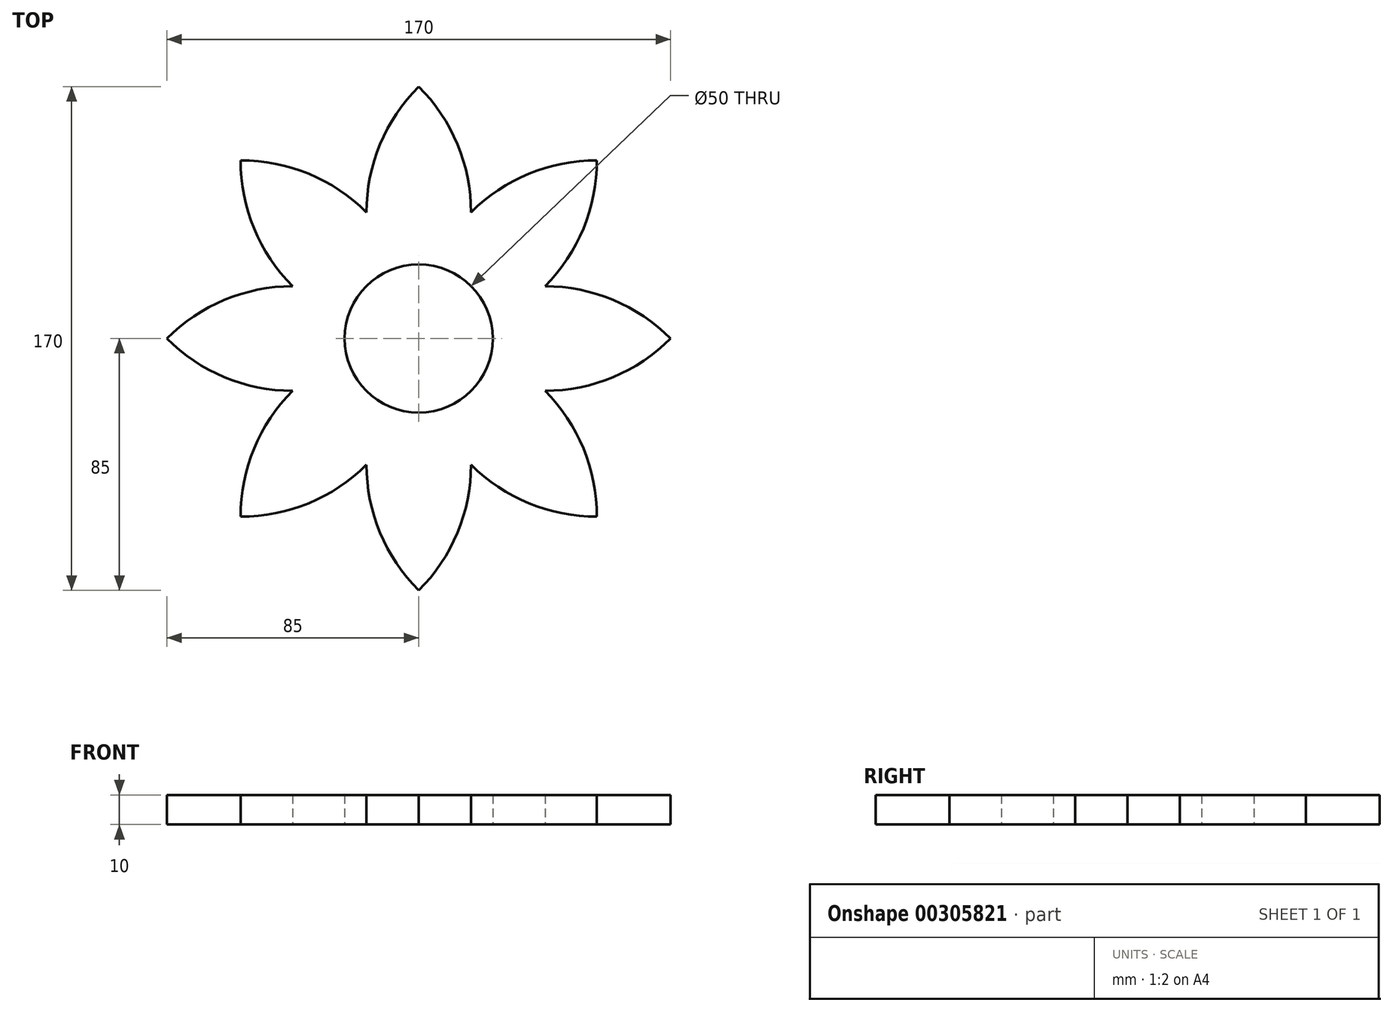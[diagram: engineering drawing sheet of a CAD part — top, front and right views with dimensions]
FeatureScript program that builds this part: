
annotation { "Feature Type Name" : "Feature", "Feature Type Description" : "" }
export const myFeature = defineFeature(function(context is Context, id is Id, definition is map)
    precondition{}
    {
        {
            var Q0;
            Q0=qCreatedBy(makeId("Top.planeOp"),FACE);
            var sketch = newSketch(context, id + "F0", { "sketchPlane" : qUnion([Q0])});
            skCircle(sketch, "E0", {"center": v(0, 0) * mm, "radius": 25 * mm});
            skLineSegment(sketch, "E1", {"start": v(0, 25) * mm, "end": v(0, 85) * mm});
            skArc(sketch, "E2", {"start": v(0, 85) * mm, "mid": v(-17.65, 42.5) * mm, "end": v(0, 0) * mm});
            skArc(sketch, "E3.MirrorCS", {"start": v(0, 85) * mm, "mid": v(17.65, 42.5) * mm, "end": v(0, 0) * mm});
            skArc(sketch, "E4.1.0", {"start": v(-60.1, 60.1) * mm, "mid": v(-17.57, 42.53) * mm, "end": v(0, 0) * mm});
            skLineSegment(sketch, "E4.1.1", {"start": v(-17.68, 17.68) * mm, "end": v(-60.1, 60.1) * mm});
            skArc(sketch, "E4.1.2", {"start": v(-60.1, 60.1) * mm, "mid": v(-42.53, 17.57) * mm, "end": v(0, 0) * mm});
            skArc(sketch, "E4.1.3", {"start": v(-60.1, 60.1) * mm, "mid": v(-17.57, 42.53) * mm, "end": v(0, 0) * mm});
            skArc(sketch, "E4.2.0", {"start": v(-85, 0) * mm, "mid": v(-42.5, 17.65) * mm, "end": v(0, 0) * mm});
            skLineSegment(sketch, "E4.2.1", {"start": v(-25, 0) * mm, "end": v(-85, 0) * mm});
            skArc(sketch, "E4.2.2", {"start": v(-85, 0) * mm, "mid": v(-42.5, -17.65) * mm, "end": v(0, 0) * mm});
            skArc(sketch, "E4.2.3", {"start": v(-85, 0) * mm, "mid": v(-42.5, 17.65) * mm, "end": v(0, 0) * mm});
            skArc(sketch, "E4.3.0", {"start": v(-60.1, -60.1) * mm, "mid": v(-42.53, -17.57) * mm, "end": v(0, 0) * mm});
            skLineSegment(sketch, "E4.3.1", {"start": v(-17.68, -17.68) * mm, "end": v(-60.1, -60.1) * mm});
            skArc(sketch, "E4.3.2", {"start": v(-60.1, -60.1) * mm, "mid": v(-17.57, -42.53) * mm, "end": v(0, 0) * mm});
            skArc(sketch, "E4.3.3", {"start": v(-60.1, -60.1) * mm, "mid": v(-42.53, -17.57) * mm, "end": v(0, 0) * mm});
            skArc(sketch, "E4.4.0", {"start": v(0, -85) * mm, "mid": v(-17.65, -42.5) * mm, "end": v(0, 0) * mm});
            skLineSegment(sketch, "E4.4.1", {"start": v(0, -25) * mm, "end": v(0, -85) * mm});
            skArc(sketch, "E4.4.2", {"start": v(0, -85) * mm, "mid": v(17.65, -42.5) * mm, "end": v(0, 0) * mm});
            skArc(sketch, "E4.4.3", {"start": v(0, -85) * mm, "mid": v(-17.65, -42.5) * mm, "end": v(0, 0) * mm});
            skArc(sketch, "E4.5.0", {"start": v(60.1, -60.1) * mm, "mid": v(17.57, -42.53) * mm, "end": v(0, 0) * mm});
            skLineSegment(sketch, "E4.5.1", {"start": v(17.68, -17.68) * mm, "end": v(60.1, -60.1) * mm});
            skArc(sketch, "E4.5.2", {"start": v(60.1, -60.1) * mm, "mid": v(42.53, -17.57) * mm, "end": v(0, 0) * mm});
            skArc(sketch, "E4.5.3", {"start": v(60.1, -60.1) * mm, "mid": v(17.57, -42.53) * mm, "end": v(0, 0) * mm});
            skArc(sketch, "E4.6.0", {"start": v(85, 0) * mm, "mid": v(42.5, -17.65) * mm, "end": v(0, 0) * mm});
            skLineSegment(sketch, "E4.6.1", {"start": v(25, 0) * mm, "end": v(85, 0) * mm});
            skArc(sketch, "E4.6.2", {"start": v(85, 0) * mm, "mid": v(42.5, 17.65) * mm, "end": v(0, 0) * mm});
            skArc(sketch, "E4.6.3", {"start": v(85, 0) * mm, "mid": v(42.5, -17.65) * mm, "end": v(0, 0) * mm});
            skArc(sketch, "E4.7.0", {"start": v(60.1, 60.1) * mm, "mid": v(42.53, 17.57) * mm, "end": v(0, 0) * mm});
            skLineSegment(sketch, "E4.7.1", {"start": v(17.68, 17.68) * mm, "end": v(60.1, 60.1) * mm});
            skArc(sketch, "E4.7.2", {"start": v(60.1, 60.1) * mm, "mid": v(17.57, 42.53) * mm, "end": v(0, 0) * mm});
            skArc(sketch, "E4.7.3", {"start": v(60.1, 60.1) * mm, "mid": v(42.53, 17.57) * mm, "end": v(0, 0) * mm});
            skSolve(sketch);
        }
        {
            var Q0;
            Q0 = qSketchRegion(id + "F0", true);
            extrude(context, id + "F1", {"entities" : qUnion([Q0]), "depth" : 10 * mm});
        }
    });
